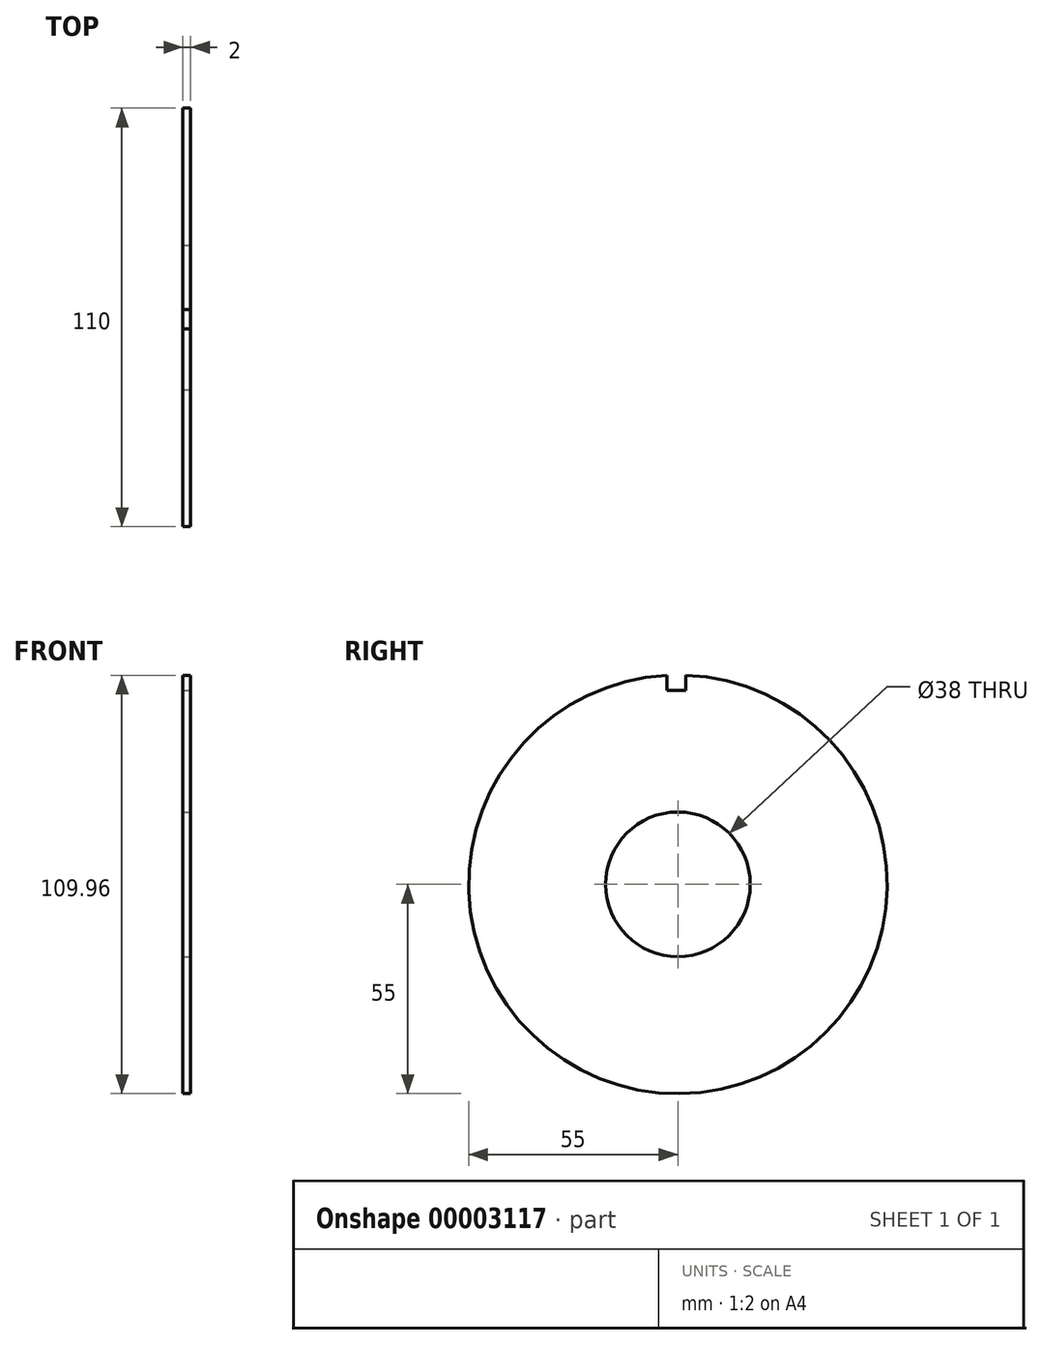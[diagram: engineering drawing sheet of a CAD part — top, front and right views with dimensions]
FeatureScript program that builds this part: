
annotation { "Feature Type Name" : "Feature", "Feature Type Description" : "" }
export const myFeature = defineFeature(function(context is Context, id is Id, definition is map)
    precondition{}
    {
        {
            var Q0;
            Q0=qCreatedBy(makeId("Right.planeOp"),FACE);
            var sketch = newSketch(context, id + "F0", { "sketchPlane" : qUnion([Q0])});
            skCircle(sketch, "E0", {"center": v(0, 0) * mm, "radius": 19 * mm});
            skCircle(sketch, "E1", {"center": v(0, 0) * mm, "radius": 55 * mm});
            skSolve(sketch);
        }
        {
            var Q0;
            Q0=makeQuery(id+"F0.imprint","IMPRINT",FACE,{"disambiguationData":[TD([[makeQuery(id+"F0.imprint","IMPRINT",EDGE,{"derivedFrom":sQuery(id+"F0.wireOp",EDGE,"E0")}),-1.0]])]});
            extrude(context, id + "F1", {"entities" : qUnion([Q0]), "oppositeDirection" : true, "depth" : 2 * mm});
        }
        {
            var Q0;
            Q0=makeQuery(id+"F1.opExtrude","CAP_FACE",FACE,{"disambiguationData":[OSD([sQuery(id+"F0.wireOp",EDGE,"E0"),sQuery(id+"F0.wireOp",EDGE,"E1")])],"isStart":true});
            var sketch = newSketch(context, id + "F2", { "sketchPlane" : qUnion([Q0])});
            skLineSegment(sketch, "E2", {"start": v(-2.95, 54.92) * mm, "end": v(-2.95, 50.96) * mm});
            skLineSegment(sketch, "E3", {"start": v(-2.95, 50.96) * mm, "end": v(2.05, 50.96) * mm});
            skLineSegment(sketch, "E4", {"start": v(2.05, 50.96) * mm, "end": v(2.05, 54.96) * mm});
            skSolve(sketch);
        }
        {
            var Q0;
            {var subQ2=sQuery(id+"F2.wireOp",EDGE,"E2");Q0=makeQuery(id+"F2.imprint","IMPRINT",FACE,{"disambiguationData":[TD([[makeQuery(id+"F2.imprint","IMPRINT",EDGE,{"derivedFrom":subQ2}),1.0]])]});}
            var Q1;
            Q1=makeQuery(id+"F2.imprint","IMPRINT",FACE,{"disambiguationData":[TD([[makeQuery(id+"F2.imprint","IMPRINT",EDGE,{"derivedFrom":sQuery(id+"F2.wireOp",EDGE,"1b97c39c-4ac7-43f6-9967-95967a36a85a")}),1.0]])]});
            var Q2;
            {var subQ2=sQuery(id+"F2.wireOp",EDGE,"7f88d279-3159-42c6-8516-7ed1a7187579");Q2=makeQuery(id+"F2.imprint","IMPRINT",FACE,{"disambiguationData":[TD([[makeQuery(id+"F2.imprint","IMPRINT",EDGE,{"derivedFrom":subQ2}),-1.0]])]});}
            var Q3;
            {var subQ2=sQuery(id+"F2.wireOp",EDGE,"159cd603-0d46-4294-aa9a-f3e4db254a6b");Q3=makeQuery(id+"F2.imprint","IMPRINT",FACE,{"disambiguationData":[TD([[makeQuery(id+"F2.imprint","IMPRINT",EDGE,{"derivedFrom":subQ2}),-1.0]])]});}
            extrude(context, id + "F3", {"entities" : qUnion([Q0, Q1, Q2, Q3]), "operationType" : NewBodyOperationType.REMOVE, "endBound" : BoundingType.UP_TO_NEXT, "oppositeDirection" : true, "depth" : 25 * mm});
        }
    });
